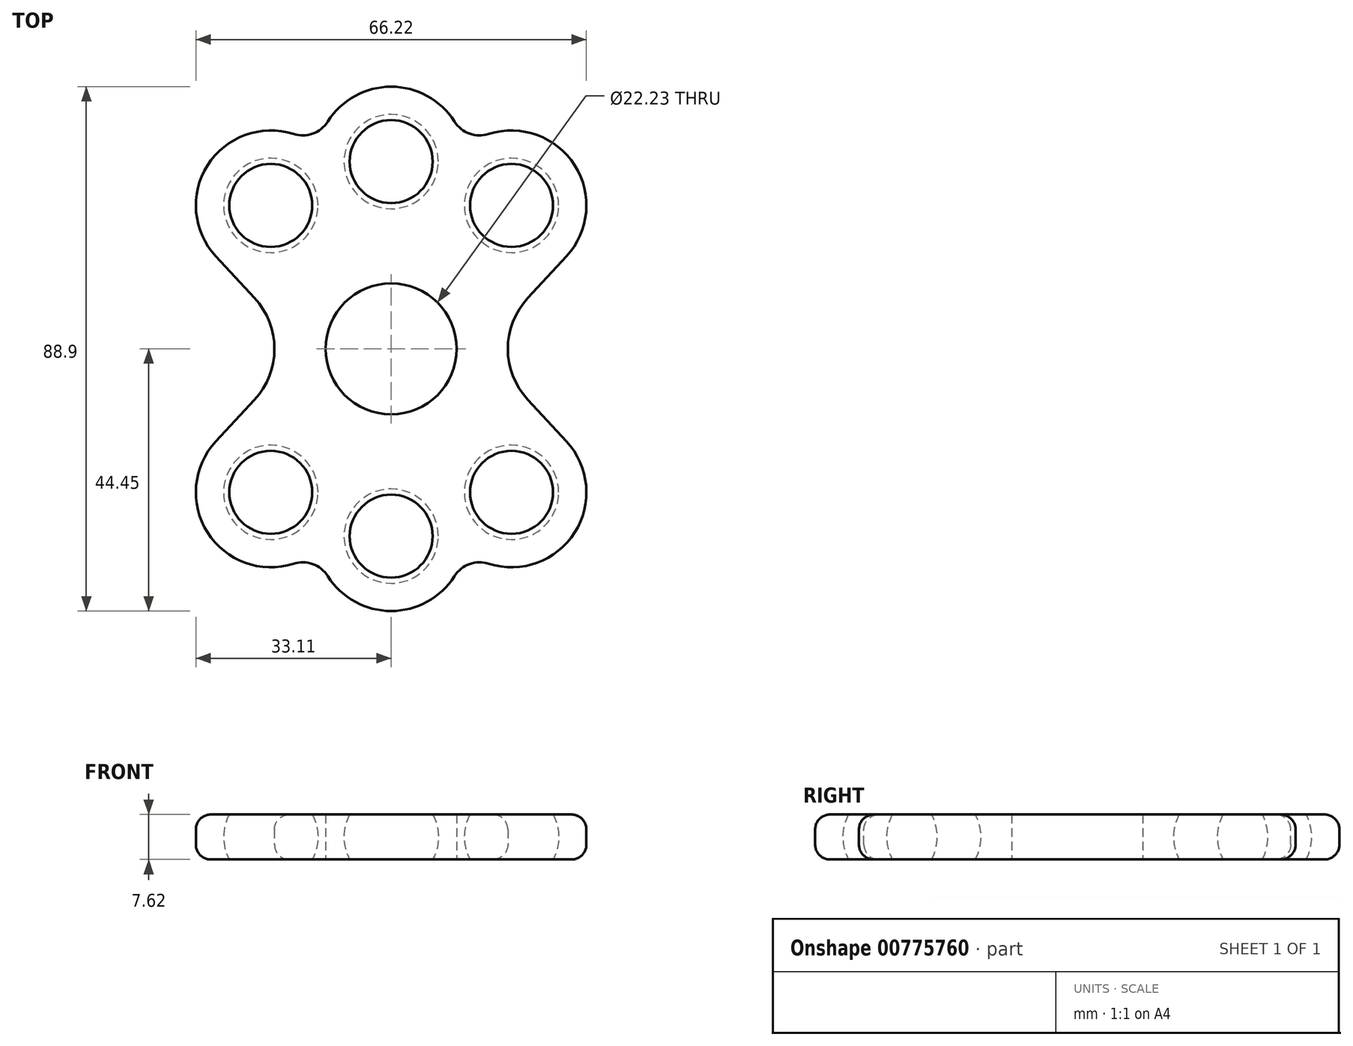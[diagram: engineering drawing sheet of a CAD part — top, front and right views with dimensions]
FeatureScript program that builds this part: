
annotation { "Feature Type Name" : "Feature", "Feature Type Description" : "" }
export const myFeature = defineFeature(function(context is Context, id is Id, definition is map)
    precondition{}
    {
        {
            var Q0;
            Q0=qCreatedBy(makeId("Top.planeOp"),FACE);
            var sketch = newSketch(context, id + "F0", { "sketchPlane" : qUnion([Q0])});
            skLineSegment(sketch, "E0", {"start": v(0, 31.75) * mm, "end": v(0, 0) * mm, "construction": true});
            skLineSegment(sketch, "E1", {"start": v(0, 0) * mm, "end": v(42.14, 0) * mm, "construction": true});
            skLineSegment(sketch, "E2", {"start": v(0, 31.75) * mm, "end": v(0, 57.84) * mm, "construction": true});
            skLineSegment(sketch, "E3", {"start": v(0, 0) * mm, "end": v(20.4, 24.32) * mm, "construction": true});
            skCircle(sketch, "E4", {"center": v(0, 0) * mm, "radius": 11.11 * mm});
            skArc(sketch, "E5", {"start": v(0, 23.75) * mm, "mid": v(8, 31.75) * mm, "end": v(0, 39.75) * mm, "construction": true});
            skCircle(sketch, "E6", {"center": v(20.4, 24.32) * mm, "radius": 8 * mm, "construction": true});
            skArc(sketch, "E7", {"start": v(29.72, 15.68) * mm, "mid": v(29.7, 32.98) * mm, "end": v(12.46, 34.22) * mm});
            skLineSegment(sketch, "E8", {"start": v(29.72, 15.68) * mm, "end": v(15.16, 0) * mm});
            skArc(sketch, "E9.MirrorCS", {"start": v(0, 23.75) * mm, "mid": v(-8, 31.75) * mm, "end": v(0, 39.75) * mm, "construction": true});
            skArc(sketch, "E10.MirrorC", {"start": v(-29.72, 15.68) * mm, "mid": v(-29.7, 32.98) * mm, "end": v(-12.46, 34.22) * mm});
            skCircle(sketch, "E11.MirrorC", {"center": v(-20.4, 24.32) * mm, "radius": 8 * mm, "construction": true});
            skLineSegment(sketch, "E12.MirrorCS", {"start": v(-29.72, 15.68) * mm, "end": v(-15.16, 0) * mm});
            skLineSegment(sketch, "E13.MirrorCS", {"start": v(29.72, -15.68) * mm, "end": v(15.16, 0) * mm});
            skLineSegment(sketch, "E14.MirrorCS", {"start": v(-29.72, -15.68) * mm, "end": v(-15.16, 0) * mm});
            skArc(sketch, "E15.MirrorC", {"start": v(-29.72, -15.68) * mm, "mid": v(-29.7, -32.98) * mm, "end": v(-12.46, -34.22) * mm});
            skArc(sketch, "E16.MirrorCS", {"start": v(-12.46, -34.22) * mm, "mid": v(-8.06, -41.57) * mm, "end": v(0, -44.45) * mm});
            skArc(sketch, "E17.MirrorC", {"start": v(29.72, -15.68) * mm, "mid": v(29.7, -32.98) * mm, "end": v(12.46, -34.22) * mm});
            skPoint(sketch, "E18.orphan", {"position": v(-8.14, 7.56) * mm});
            skPoint(sketch, "E19.orphan", {"position": v(-8.14, -7.56) * mm});
            skPoint(sketch, "E20.orphan", {"position": v(8.14, -7.56) * mm});
            skPoint(sketch, "E21.orphan", {"position": v(8.14, 7.56) * mm});
            skArc(sketch, "E22.trimOffspring", {"start": v(-12.46, 34.22) * mm, "mid": v(-8.06, 41.57) * mm, "end": v(0, 44.45) * mm});
            skArc(sketch, "E23.trimOffspring", {"start": v(12.46, 34.22) * mm, "mid": v(8.06, 41.57) * mm, "end": v(0, 44.45) * mm});
            skArc(sketch, "E24.trimOffspring", {"start": v(12.46, -34.22) * mm, "mid": v(8.06, -41.57) * mm, "end": v(0, -44.45) * mm});
            skPoint(sketch, "E25.MirrorCS.start.orphan", {"position": v(0, -19.05) * mm});
            skPoint(sketch, "E26.MirrorCS.start.orphan", {"position": v(0, 19.05) * mm});
            skSolve(sketch);
        }
        {
            var Q0;
            Q0 = qSketchRegion(id + "F0", true);
            extrude(context, id + "F1", {"entities" : qUnion([Q0]), "endBound" : BoundingType.SYMMETRIC, "depth" : 7.62 * mm, "offsetDistance" : 25.4 * mm});
        }
        {
            var Q0;
            Q0=qCreatedBy(makeId("Front.planeOp"),FACE);
            var sketch = newSketch(context, id + "F2", { "sketchPlane" : qUnion([Q0])});
            skLineSegment(sketch, "E27", {"start": v(0, 0) * mm, "end": v(0, 93.09) * mm});
            skSolve(sketch);
        }
        {
            var Q0;
            Q0=sQuery(id+"F0.wireOp",VERTEX,"E3.end");
            var Q1;
            Q1=sQuery(id+"F2.wireOp",VERTEX,"E27.end");
            var Q2;
            Q2=sQuery(id+"F0.wireOp",VERTEX,"E0.end");
            cPlane(context, id + "F3", {"entities" : qUnion([Q0, Q1, Q2]), "cplaneType" : CPlaneType.THREE_POINT, "offset" : 25.4 * mm, "width" : 152.4 * mm, "height" : 152.4 * mm});
        }
        {
            var Q0;
            Q0=qCreatedBy(id+"F3.planeOp",FACE);
            var sketch = newSketch(context, id + "F4", { "sketchPlane" : qUnion([Q0])});
            skLineSegment(sketch, "E28", {"start": v(-31.75, 0) * mm, "end": v(-31.75, 45.58) * mm, "construction": true});
            skLineSegment(sketch, "E29", {"start": v(-31.75, 8) * mm, "end": v(-31.75, -8) * mm});
            skArc(sketch, "E30", {"start": v(-31.75, 8) * mm, "mid": v(-39.75, 0) * mm, "end": v(-31.75, -8) * mm});
            skSolve(sketch);
        }
        {
            var Q0;
            Q0 = qSketchRegion(id + "F4", true);
            var Q1;
            Q1=sQuery(id+"F4.wireOp",EDGE,"E28");
            revolve(context, id + "F5", {"surfaceOperationType" : NewSurfaceOperationType.NEW, "entities" : qUnion([Q0]), "axis" : qUnion([Q1]), "revolveType" : RevolveType.FULL});
        }
        {
            var Q0;
            Q0=qCreatedBy(makeId("Right.planeOp"),FACE);
            var sketch = newSketch(context, id + "F6", { "sketchPlane" : qUnion([Q0])});
            skLineSegment(sketch, "E31", {"start": v(31.75, 0) * mm, "end": v(31.75, 41) * mm, "construction": true});
            skLineSegment(sketch, "E32", {"start": v(31.75, 8) * mm, "end": v(31.75, -8) * mm});
            skArc(sketch, "E33", {"start": v(31.75, -8) * mm, "mid": v(39.75, 0) * mm, "end": v(31.75, 8) * mm});
            skSolve(sketch);
        }
        {
            var Q0;
            Q0=makeQuery(id+"F6.imprint","IMPRINT",FACE,{"disambiguationData":[TD([[makeQuery(id+"F6.imprint","IMPRINT",EDGE,{"derivedFrom":sQuery(id+"F6.wireOp",EDGE,"E32")}),1.0]])]});
            var Q1;
            Q1=sQuery(id+"F6.wireOp",EDGE,"E31");
            revolve(context, id + "F7", {"surfaceOperationType" : NewSurfaceOperationType.NEW, "entities" : qUnion([Q0]), "axis" : qUnion([Q1]), "revolveType" : RevolveType.FULL});
        }
        {
            var Q0;
            Q0=makeQuery(id+"F5.opRevolve","SWEPT_BODY",BODY,{"disambiguationData":[OSD([sQuery(id+"F4.wireOp",EDGE,"E29"),sQuery(id+"F4.wireOp",EDGE,"E30")])]});
            var Q1;
            Q1=qCreatedBy(makeId("Right.planeOp"),FACE);
            mirror(context, id + "F8", {"entities" : qUnion([Q0]), "mirrorPlane" : qUnion([Q1])});
        }
        {
            var Q0;
            Q0=makeQuery(id+"F8.opPattern","COPY",BODY,{"derivedFrom":makeQuery(id+"F5.opRevolve","SWEPT_BODY",BODY,{"disambiguationData":[OSD([sQuery(id+"F4.wireOp",EDGE,"E29"),sQuery(id+"F4.wireOp",EDGE,"E30")])]}),"instanceName":"1"});
            var Q1;
            Q1=makeQuery(id+"F7.opRevolve","SWEPT_BODY",BODY,{"disambiguationData":[OSD([sQuery(id+"F6.wireOp",EDGE,"E32"),sQuery(id+"F6.wireOp",EDGE,"E33")])]});
            var Q2;
            Q2=makeQuery(id+"F5.opRevolve","SWEPT_BODY",BODY,{"disambiguationData":[OSD([sQuery(id+"F4.wireOp",EDGE,"E29"),sQuery(id+"F4.wireOp",EDGE,"E30")])]});
            var Q3;
            Q3=qCreatedBy(makeId("Front.planeOp"),FACE);
            mirror(context, id + "F9", {"entities" : qUnion([Q0, Q1, Q2]), "mirrorPlane" : qUnion([Q3])});
        }
        {
            var Q0;
            Q0=makeQuery(id+"F9.opPattern","COPY",BODY,{"derivedFrom":makeQuery(id+"F8.opPattern","COPY",BODY,{"derivedFrom":makeQuery(id+"F5.opRevolve","SWEPT_BODY",BODY,{"disambiguationData":[OSD([sQuery(id+"F4.wireOp",EDGE,"E29"),sQuery(id+"F4.wireOp",EDGE,"E30")])]}),"instanceName":"1"}),"instanceName":"1"});
            var Q1;
            Q1=makeQuery(id+"F9.opPattern","COPY",BODY,{"derivedFrom":makeQuery(id+"F7.opRevolve","SWEPT_BODY",BODY,{"disambiguationData":[OSD([sQuery(id+"F6.wireOp",EDGE,"E32"),sQuery(id+"F6.wireOp",EDGE,"E33")])]}),"instanceName":"1"});
            var Q2;
            Q2=makeQuery(id+"F9.opPattern","COPY",BODY,{"derivedFrom":makeQuery(id+"F5.opRevolve","SWEPT_BODY",BODY,{"disambiguationData":[OSD([sQuery(id+"F4.wireOp",EDGE,"E29"),sQuery(id+"F4.wireOp",EDGE,"E30")])]}),"instanceName":"1"});
            var Q3;
            Q3=makeQuery(id+"F8.opPattern","COPY",BODY,{"derivedFrom":makeQuery(id+"F5.opRevolve","SWEPT_BODY",BODY,{"disambiguationData":[OSD([sQuery(id+"F4.wireOp",EDGE,"E29"),sQuery(id+"F4.wireOp",EDGE,"E30")])]}),"instanceName":"1"});
            var Q4;
            Q4=makeQuery(id+"F5.opRevolve","SWEPT_BODY",BODY,{"disambiguationData":[OSD([sQuery(id+"F4.wireOp",EDGE,"E29"),sQuery(id+"F4.wireOp",EDGE,"E30")])]});
            var Q5;
            Q5=makeQuery(id+"F7.opRevolve","SWEPT_BODY",BODY,{"disambiguationData":[OSD([sQuery(id+"F6.wireOp",EDGE,"E32"),sQuery(id+"F6.wireOp",EDGE,"E33")])]});
            var Q6;
            Q6=makeQuery(id+"F1.opExtrude","SWEPT_BODY",BODY,{"disambiguationData":[OSD([sQuery(id+"F0.wireOp",EDGE,"E4"),sQuery(id+"F0.wireOp",EDGE,"E7"),sQuery(id+"F0.wireOp",EDGE,"E8"),sQuery(id+"F0.wireOp",EDGE,"E10.MirrorC"),sQuery(id+"F0.wireOp",EDGE,"E12.MirrorCS"),sQuery(id+"F0.wireOp",EDGE,"E13.MirrorCS"),sQuery(id+"F0.wireOp",EDGE,"E14.MirrorCS"),sQuery(id+"F0.wireOp",EDGE,"E15.MirrorC"),sQuery(id+"F0.wireOp",EDGE,"E16.MirrorCS"),sQuery(id+"F0.wireOp",EDGE,"E17.MirrorC"),sQuery(id+"F0.wireOp",EDGE,"E22.trimOffspring"),sQuery(id+"F0.wireOp",EDGE,"E23.trimOffspring"),sQuery(id+"F0.wireOp",EDGE,"E24.trimOffspring")])]});
            booleanBodies(context, id + "F10", {"operationType" : BooleanOperationType.SUBTRACTION, "tools" : qUnion([Q0, Q1, Q2, Q3, Q4, Q5]), "targets" : qUnion([Q6])});
        }
        {
            var Q0;
            Q0=makeQuery(id+"F1.opExtrude","SWEPT_EDGE",EDGE,{"disambiguationData":[OSD([sQuery(id+"F0.wireOp",EDGE,"E8"),sQuery(id+"F0.wireOp",EDGE,"E13.MirrorCS")])]});
            var Q1;
            Q1=makeQuery(id+"F1.opExtrude","SWEPT_EDGE",EDGE,{"disambiguationData":[OSD([sQuery(id+"F0.wireOp",EDGE,"E12.MirrorCS"),sQuery(id+"F0.wireOp",EDGE,"E14.MirrorCS")])]});
            fillet(context, id + "F11", {"entities" : qUnion([Q0, Q1]), "radius" : 12.7 * mm, "tangentPropagation" : true, "allowEdgeOverflow" : false});
        }
        {
            var Q0;
            Q0=makeQuery(id+"F1.opExtrude","SWEPT_EDGE",EDGE,{"disambiguationData":[OSD([sQuery(id+"F0.wireOp",EDGE,"E15.MirrorC"),sQuery(id+"F0.wireOp",EDGE,"E16.MirrorCS")])]});
            var Q1;
            Q1=makeQuery(id+"F1.opExtrude","SWEPT_EDGE",EDGE,{"disambiguationData":[OSD([sQuery(id+"F0.wireOp",EDGE,"E17.MirrorC"),sQuery(id+"F0.wireOp",EDGE,"E24.trimOffspring")])]});
            var Q2;
            Q2=makeQuery(id+"F1.opExtrude","SWEPT_EDGE",EDGE,{"disambiguationData":[OSD([sQuery(id+"F0.wireOp",EDGE,"E7"),sQuery(id+"F0.wireOp",EDGE,"E23.trimOffspring")])]});
            var Q3;
            Q3=makeQuery(id+"F1.opExtrude","SWEPT_EDGE",EDGE,{"disambiguationData":[OSD([sQuery(id+"F0.wireOp",EDGE,"E10.MirrorC"),sQuery(id+"F0.wireOp",EDGE,"E22.trimOffspring")])]});
            fillet(context, id + "F12", {"entities" : qUnion([Q0, Q1, Q2, Q3]), "radius" : 5.08 * mm, "tangentPropagation" : true, "allowEdgeOverflow" : false});
        }
        {
            var Q0;
            {var subQ0=sQuery(id+"F0.wireOp",EDGE,"E13.MirrorCS");var subQ1=sQuery(id+"F0.wireOp",EDGE,"E8");Q0=makeQuery(id+"F11.opFillet","BLEND_EDGE",EDGE,{"blendedFrom":[makeQuery(id+"F1.opExtrude","SWEPT_EDGE",EDGE,{"disambiguationData":[OSD([subQ1,subQ0])]}),makeQuery(id+"F1.opExtrude","CAP_FACE",FACE,{"disambiguationData":[OSD([sQuery(id+"F0.wireOp",EDGE,"E4"),sQuery(id+"F0.wireOp",EDGE,"E7"),subQ1,sQuery(id+"F0.wireOp",EDGE,"E10.MirrorC"),sQuery(id+"F0.wireOp",EDGE,"E12.MirrorCS"),subQ0,sQuery(id+"F0.wireOp",EDGE,"E14.MirrorCS"),sQuery(id+"F0.wireOp",EDGE,"E15.MirrorC"),sQuery(id+"F0.wireOp",EDGE,"E16.MirrorCS"),sQuery(id+"F0.wireOp",EDGE,"E17.MirrorC"),sQuery(id+"F0.wireOp",EDGE,"E22.trimOffspring"),sQuery(id+"F0.wireOp",EDGE,"E23.trimOffspring"),sQuery(id+"F0.wireOp",EDGE,"E24.trimOffspring")])],"isStart":false})],"blendedInto":[makeQuery(id+"F1.opExtrude","CAP_FACE",FACE,{"disambiguationData":[OSD([sQuery(id+"F0.wireOp",EDGE,"E4"),sQuery(id+"F0.wireOp",EDGE,"E7"),subQ1,sQuery(id+"F0.wireOp",EDGE,"E10.MirrorC"),sQuery(id+"F0.wireOp",EDGE,"E12.MirrorCS"),subQ0,sQuery(id+"F0.wireOp",EDGE,"E14.MirrorCS"),sQuery(id+"F0.wireOp",EDGE,"E15.MirrorC"),sQuery(id+"F0.wireOp",EDGE,"E16.MirrorCS"),sQuery(id+"F0.wireOp",EDGE,"E17.MirrorC"),sQuery(id+"F0.wireOp",EDGE,"E22.trimOffspring"),sQuery(id+"F0.wireOp",EDGE,"E23.trimOffspring"),sQuery(id+"F0.wireOp",EDGE,"E24.trimOffspring")])],"isStart":false})]});}
            var Q1;
            Q1=makeQuery(id+"F1.opExtrude","CAP_EDGE",EDGE,{"disambiguationData":[OSD([sQuery(id+"F0.wireOp",EDGE,"E17.MirrorC")])],"isStart":true});
            var Q2;
            Q2=makeQuery(id+"F1.opExtrude","CAP_EDGE",EDGE,{"disambiguationData":[OSD([sQuery(id+"F0.wireOp",EDGE,"E13.MirrorCS")])],"isStart":true});
            fillet(context, id + "F13", {"entities" : qUnion([Q0, Q1, Q2]), "radius" : 2.54 * mm, "tangentPropagation" : true, "allowEdgeOverflow" : false});
        }
    });
